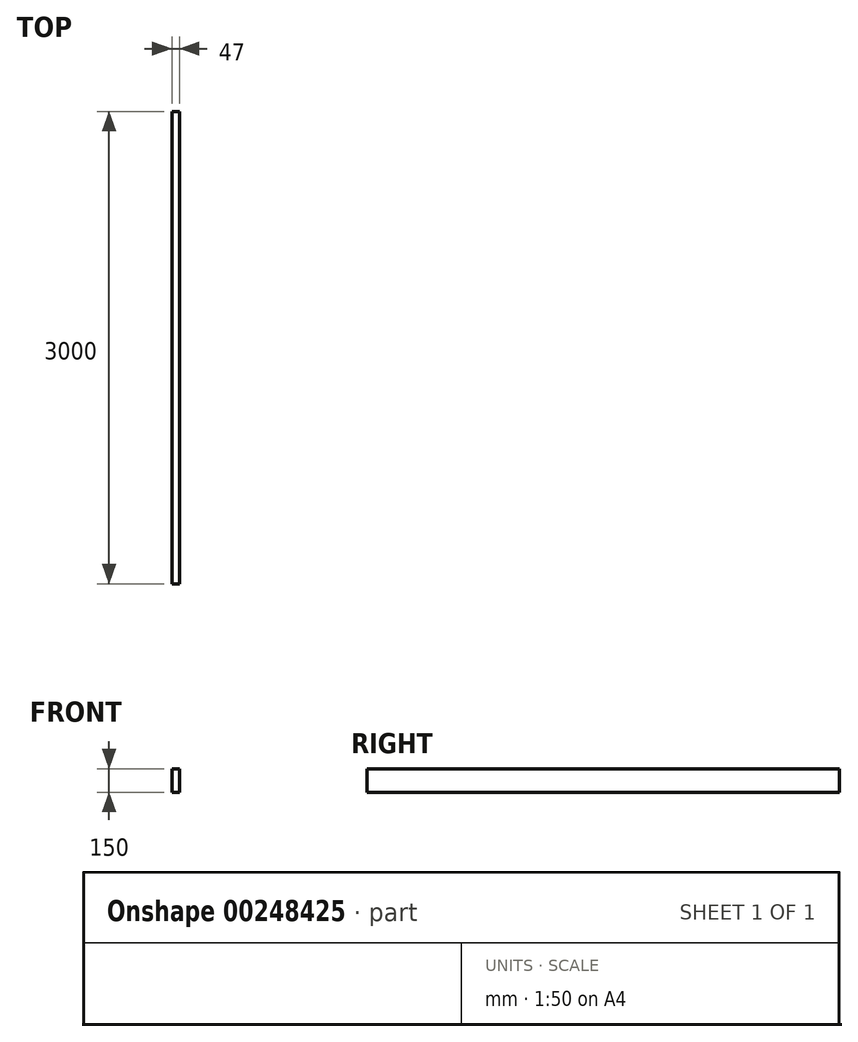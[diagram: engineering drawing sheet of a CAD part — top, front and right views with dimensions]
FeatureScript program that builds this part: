
annotation { "Feature Type Name" : "Feature", "Feature Type Description" : "" }
export const myFeature = defineFeature(function(context is Context, id is Id, definition is map)
    precondition{}
    {
        {
            var Q0;
            Q0=qCreatedBy(makeId("Front.planeOp"),FACE);
            var sketch = newSketch(context, id + "F0", { "sketchPlane" : qUnion([Q0])});
            skLineSegment(sketch, "E0.bottom", {"start": v(0, 0) * mm, "end": v(47, 0) * mm});
            skLineSegment(sketch, "E0.top", {"start": v(0, 150) * mm, "end": v(47, 150) * mm});
            skLineSegment(sketch, "E0.left", {"start": v(0, 0) * mm, "end": v(0, 150) * mm});
            skLineSegment(sketch, "E0.right", {"start": v(47, 0) * mm, "end": v(47, 150) * mm});
            skSolve(sketch);
        }
        {
            var Q0;
            Q0=makeQuery(id+"F0.imprint","IMPRINT",FACE,{"disambiguationData":[TD([[makeQuery(id+"F0.imprint","IMPRINT",EDGE,{"derivedFrom":sQuery(id+"F0.wireOp",EDGE,"E0.bottom")}),1.0]])]});
            extrude(context, id + "F1", {"entities" : qUnion([Q0]), "oppositeDirection" : true, "depth" : 3000 * mm});
        }
    });
